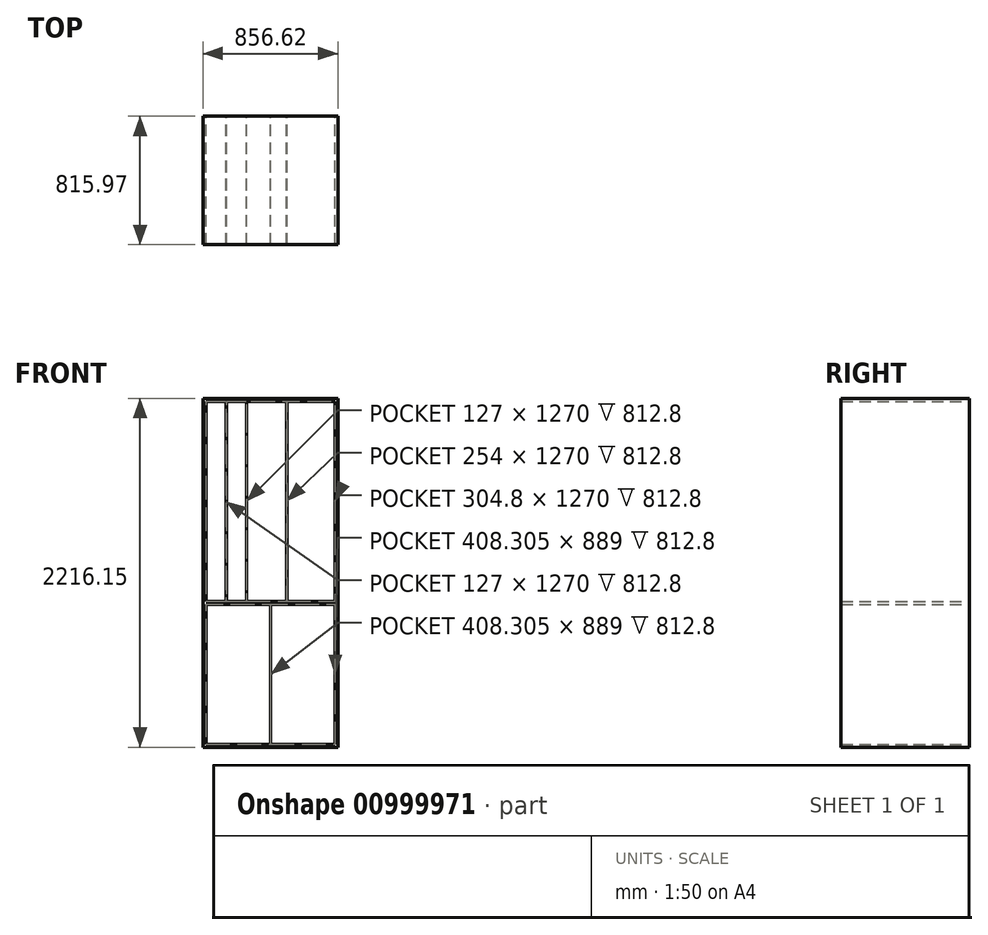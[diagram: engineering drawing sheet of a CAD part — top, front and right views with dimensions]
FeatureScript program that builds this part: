
annotation { "Feature Type Name" : "Feature", "Feature Type Description" : "" }
export const myFeature = defineFeature(function(context is Context, id is Id, definition is map)
    precondition{}
    {
        {
            var Q0;
            Q0=qCreatedBy(makeId("Front.planeOp"),FACE);
            var sketch = newSketch(context, id + "F0", { "sketchPlane" : qUnion([Q0])});
            skLineSegment(sketch, "E0.bottom", {"start": v(-409.26, 1098.55) * mm, "end": v(409.26, 1098.55) * mm});
            skLineSegment(sketch, "E0.top", {"start": v(-409.26, -1098.55) * mm, "end": v(409.26, -1098.55) * mm});
            skLineSegment(sketch, "E0.left", {"start": v(-409.26, 1098.55) * mm, "end": v(-409.26, -1098.55) * mm});
            skLineSegment(sketch, "E0.right", {"start": v(409.26, 1098.55) * mm, "end": v(409.26, -1098.55) * mm});
            skPoint(sketch, "E0.middle", {"position": v(0, 0) * mm});
            skLineSegment(sketch, "E1", {"start": v(-409.26, -190.5) * mm, "end": v(409.26, -190.5) * mm});
            skLineSegment(sketch, "E2", {"start": v(-282.26, 1098.55) * mm, "end": v(-282.26, -190.5) * mm});
            skLineSegment(sketch, "E3", {"start": v(-153.35, 1098.55) * mm, "end": v(-153.35, -190.5) * mm});
            skLineSegment(sketch, "E4", {"start": v(102.55, 1098.55) * mm, "end": v(102.55, -190.5) * mm});
            skLineSegment(sketch, "E5.left", {"start": v(409.26, -1098.55) * mm, "end": v(409.26, -342.9) * mm});
            skLineSegment(sketch, "E6.left", {"start": v(409.26, -342.9) * mm, "end": v(409.26, 419.1) * mm});
            skLineSegment(sketch, "E7.left", {"start": v(409.26, 1098.55) * mm, "end": v(409.26, 463.55) * mm});
            skLineSegment(sketch, "E8.top", {"start": v(-409.26, -1117.6) * mm, "end": v(409.26, -1117.6) * mm});
            skLineSegment(sketch, "E8.left", {"start": v(-409.26, -1098.55) * mm, "end": v(-409.26, -1117.6) * mm});
            skLineSegment(sketch, "E8.right", {"start": v(409.26, -1098.55) * mm, "end": v(409.26, -1117.6) * mm});
            skLineSegment(sketch, "E9", {"start": v(-409.26, -209.55) * mm, "end": v(409.26, -209.55) * mm});
            skLineSegment(sketch, "E10", {"start": v(-409.26, 1079.5) * mm, "end": v(409.26, 1079.5) * mm});
            skLineSegment(sketch, "E11.bottom", {"start": v(-409.26, 1098.55) * mm, "end": v(-428.3, 1098.55) * mm});
            skLineSegment(sketch, "E11.top", {"start": v(-409.26, -1117.6) * mm, "end": v(-428.3, -1117.6) * mm});
            skLineSegment(sketch, "E11.left", {"start": v(-409.26, 1098.55) * mm, "end": v(-409.26, -1117.6) * mm});
            skLineSegment(sketch, "E11.right", {"start": v(-428.3, 1098.55) * mm, "end": v(-428.3, -1117.6) * mm});
            skLineSegment(sketch, "E12.bottom", {"start": v(409.26, 1098.55) * mm, "end": v(428.3, 1098.55) * mm});
            skLineSegment(sketch, "E12.top", {"start": v(409.26, -1117.6) * mm, "end": v(428.3, -1117.6) * mm});
            skLineSegment(sketch, "E12.left", {"start": v(409.26, 1098.55) * mm, "end": v(409.26, -1117.6) * mm});
            skLineSegment(sketch, "E12.right", {"start": v(428.3, 1098.55) * mm, "end": v(428.3, -1117.6) * mm});
            skLineSegment(sketch, "E13", {"start": v(-280.35, 1079.5) * mm, "end": v(-280.35, -190.5) * mm});
            skLineSegment(sketch, "E14", {"start": v(-151.45, 1079.5) * mm, "end": v(-151.45, -190.5) * mm});
            skLineSegment(sketch, "E15", {"start": v(104.46, 1079.5) * mm, "end": v(104.46, -190.5) * mm});
            skLineSegment(sketch, "E16", {"start": v(0.95, -209.55) * mm, "end": v(0.95, -1098.55) * mm});
            skLineSegment(sketch, "E17", {"start": v(-0.95, -209.55) * mm, "end": v(-0.95, -1098.55) * mm});
            skSolve(sketch);
        }
        {
            var Q0;
            {var subQ3=sQuery(id+"F0.wireOp",EDGE,"E11.bottom");Q0=makeQuery(id+"F0.imprint","IMPRINT",FACE,{"disambiguationData":[TD([[makeQuery(id+"F0.imprint","IMPRINT",EDGE,{"derivedFrom":subQ3}),1.0]])]});}
            var Q1;
            {var subQ0=sQuery(id+"F0.wireOp",EDGE,"E8.top");Q1=makeQuery(id+"F0.imprint","IMPRINT",FACE,{"disambiguationData":[TD([[makeQuery(id+"F0.imprint","IMPRINT",EDGE,{"derivedFrom":subQ0}),1.0]])]});}
            var Q2;
            {var subQ3=sQuery(id+"F0.wireOp",EDGE,"E12.bottom");Q2=makeQuery(id+"F0.imprint","IMPRINT",FACE,{"disambiguationData":[TD([[makeQuery(id+"F0.imprint","IMPRINT",EDGE,{"derivedFrom":subQ3}),-1.0]])]});}
            var Q3;
            {var subQ1=sQuery(id+"F0.wireOp",EDGE,"E1");var subQ8=makeQuery(id+"F0.imprint","INTERSECT",VERTEX,{"derivedFrom":[subQ1,sQuery(id+"F0.wireOp",EDGE,"E4")]});Q3=makeQuery(id+"F0.imprint","IMPRINT",FACE,{"disambiguationData":[TD([[makeQuery(id+"F0.imprint","IMPRINT",EDGE,{"disambiguationData":[TD([[subQ8,1.0]])],"derivedFrom":subQ1}),-1.0]])]});}
            var Q4;
            {var subQ0=sQuery(id+"F0.wireOp",EDGE,"E1");var subQ9=sQuery(id+"F0.wireOp",EDGE,"E11.left");var subQ10=makeQuery(id+"F0.imprint","INTERSECT",VERTEX,{"derivedFrom":[subQ0,subQ9]});Q4=makeQuery(id+"F0.imprint","IMPRINT",FACE,{"disambiguationData":[TD([[makeQuery(id+"F0.imprint","IMPRINT",EDGE,{"disambiguationData":[TD([[subQ10,-1.0]])],"derivedFrom":subQ0}),-1.0]])]});}
            var Q5;
            {var subQ5=sQuery(id+"F0.wireOp",EDGE,"E16");Q5=makeQuery(id+"F0.imprint","IMPRINT",FACE,{"disambiguationData":[TD([[makeQuery(id+"F0.imprint","IMPRINT",EDGE,{"derivedFrom":subQ5}),-1.0]])]});}
            var Q6;
            {var subQ3=sQuery(id+"F0.wireOp",EDGE,"E13");Q6=makeQuery(id+"F0.imprint","IMPRINT",FACE,{"disambiguationData":[TD([[makeQuery(id+"F0.imprint","IMPRINT",EDGE,{"derivedFrom":subQ3}),-1.0]])]});}
            var Q7;
            {var subQ3=sQuery(id+"F0.wireOp",EDGE,"E14");Q7=makeQuery(id+"F0.imprint","IMPRINT",FACE,{"disambiguationData":[TD([[makeQuery(id+"F0.imprint","IMPRINT",EDGE,{"derivedFrom":subQ3}),-1.0]])]});}
            var Q8;
            {var subQ3=sQuery(id+"F0.wireOp",EDGE,"E15");Q8=makeQuery(id+"F0.imprint","IMPRINT",FACE,{"disambiguationData":[TD([[makeQuery(id+"F0.imprint","IMPRINT",EDGE,{"derivedFrom":subQ3}),-1.0]])]});}
            var Q9;
            {var subQ2=sQuery(id+"F0.wireOp",EDGE,"E3");var subQ5=sQuery(id+"F0.wireOp",EDGE,"E0.bottom");var subQ8=makeQuery(id+"F0.imprint","INTERSECT",VERTEX,{"derivedFrom":[subQ5,subQ2]});Q9=makeQuery(id+"F0.imprint","IMPRINT",FACE,{"disambiguationData":[TD([[makeQuery(id+"F0.imprint","IMPRINT",EDGE,{"disambiguationData":[TD([[subQ8,-1.0]])],"derivedFrom":subQ5}),-1.0]])]});}
            var Q10;
            {var subQ2=sQuery(id+"F0.wireOp",EDGE,"E4");var subQ4=sQuery(id+"F0.wireOp",EDGE,"E0.bottom");var subQ5=makeQuery(id+"F0.imprint","INTERSECT",VERTEX,{"derivedFrom":[subQ4,subQ2]});Q10=makeQuery(id+"F0.imprint","IMPRINT",FACE,{"disambiguationData":[TD([[makeQuery(id+"F0.imprint","IMPRINT",EDGE,{"disambiguationData":[TD([[subQ5,-1.0]])],"derivedFrom":subQ2}),1.0]])]});}
            var Q11;
            {var subQ2=sQuery(id+"F0.wireOp",EDGE,"E2");var subQ5=sQuery(id+"F0.wireOp",EDGE,"E0.bottom");var subQ8=makeQuery(id+"F0.imprint","INTERSECT",VERTEX,{"derivedFrom":[subQ5,subQ2]});Q11=makeQuery(id+"F0.imprint","IMPRINT",FACE,{"disambiguationData":[TD([[makeQuery(id+"F0.imprint","IMPRINT",EDGE,{"disambiguationData":[TD([[subQ8,-1.0]])],"derivedFrom":subQ5}),-1.0]])]});}
            var Q12;
            {var subQ1=sQuery(id+"F0.wireOp",EDGE,"E0.bottom");var subQ3=sQuery(id+"F0.wireOp",EDGE,"E2");var subQ4=makeQuery(id+"F0.imprint","INTERSECT",VERTEX,{"derivedFrom":[subQ1,subQ3]});Q12=makeQuery(id+"F0.imprint","IMPRINT",FACE,{"disambiguationData":[TD([[makeQuery(id+"F0.imprint","IMPRINT",EDGE,{"disambiguationData":[TD([[subQ4,-1.0]])],"derivedFrom":subQ3}),-1.0]])]});}
            extrude(context, id + "F1", {"entities" : qUnion([Q0, Q1, Q2, Q3, Q4, Q5, Q6, Q7, Q8, Q9, Q10, Q11, Q12]), "depth" : 812.8 * mm, "offsetDistance" : 25.4 * mm});
        }
        {
            var Q0;
            Q0=makeQuery(id+"F1.opExtrude","CAP_FACE",FACE,{"disambiguationData":[OSD([sQuery(id+"F0.wireOp",EDGE,"E0.bottom"),sQuery(id+"F0.wireOp",EDGE,"E1"),sQuery(id+"F0.wireOp",EDGE,"E2"),sQuery(id+"F0.wireOp",EDGE,"E3"),sQuery(id+"F0.wireOp",EDGE,"E4"),sQuery(id+"F0.wireOp",EDGE,"w2SEhCX0-4Wh1-OPzP-oL9h-TlErQe68mkYs"),sQuery(id+"F0.wireOp",EDGE,"E0.top"),sQuery(id+"F0.wireOp",EDGE,"E8.top"),sQuery(id+"F0.wireOp",EDGE,"E9"),sQuery(id+"F0.wireOp",EDGE,"E10"),sQuery(id+"F0.wireOp",EDGE,"E11.bottom"),sQuery(id+"F0.wireOp",EDGE,"E11.top"),sQuery(id+"F0.wireOp",EDGE,"E11.left"),sQuery(id+"F0.wireOp",EDGE,"E11.right"),sQuery(id+"F0.wireOp",EDGE,"E12.bottom"),sQuery(id+"F0.wireOp",EDGE,"E12.top"),sQuery(id+"F0.wireOp",EDGE,"E12.left"),sQuery(id+"F0.wireOp",EDGE,"E12.right"),sQuery(id+"F0.wireOp",EDGE,"E13"),sQuery(id+"F0.wireOp",EDGE,"E14"),sQuery(id+"F0.wireOp",EDGE,"E15"),sQuery(id+"F0.wireOp",EDGE,"E16")])],"isStart":true});
            var sketch = newSketch(context, id + "F2", { "sketchPlane" : qUnion([Q0])});
            skLineSegment(sketch, "E18.bottom", {"start": v(428.3, 1098.55) * mm, "end": v(-428.3, 1098.55) * mm});
            skLineSegment(sketch, "E18.top", {"start": v(428.3, -1117.6) * mm, "end": v(-428.3, -1117.6) * mm});
            skLineSegment(sketch, "E18.left", {"start": v(-428.3, -1117.6) * mm, "end": v(-428.3, 1098.55) * mm});
            skLineSegment(sketch, "E18.right", {"start": v(428.3, -1117.6) * mm, "end": v(428.3, 1098.55) * mm});
            skSolve(sketch);
        }
        {
            var Q0;
            Q0 = qSketchRegion(id + "F2", true);
            extrude(context, id + "F3", {"entities" : qUnion([Q0]), "operationType" : NewBodyOperationType.ADD, "depth" : 3.17 * mm, "offsetDistance" : 25.4 * mm});
        }
    });
